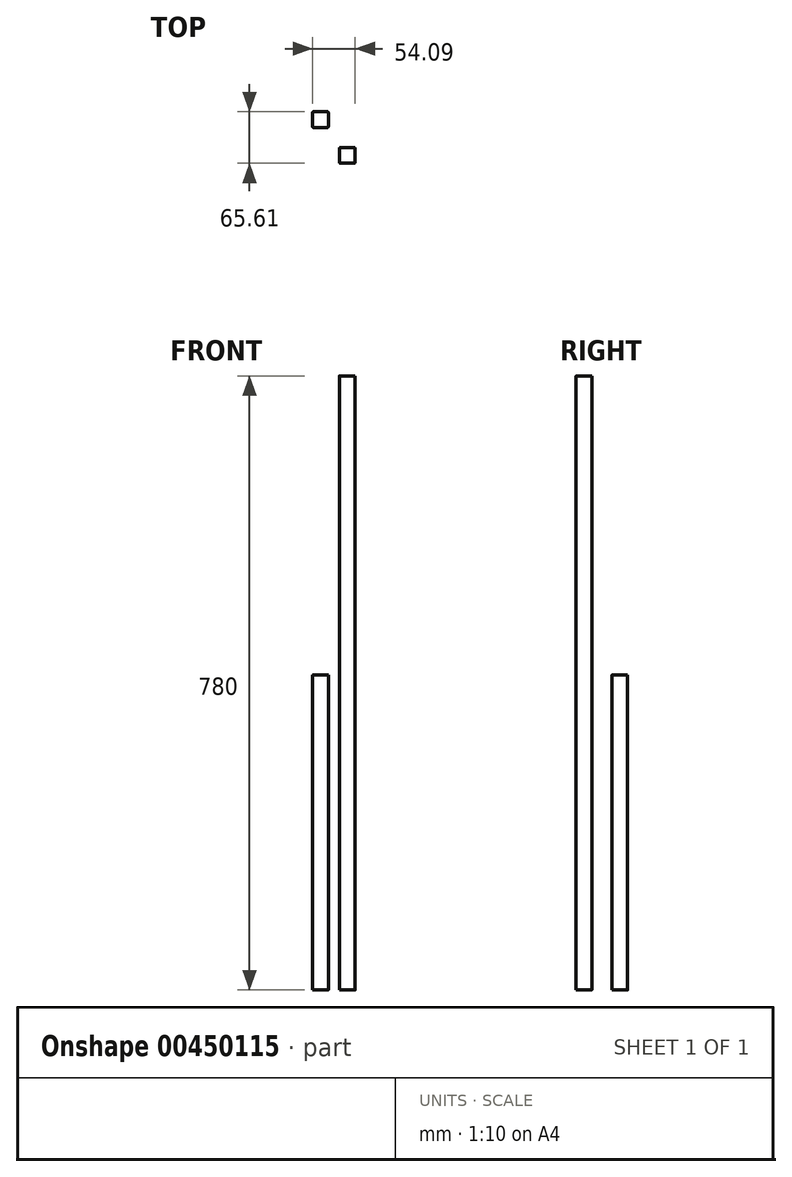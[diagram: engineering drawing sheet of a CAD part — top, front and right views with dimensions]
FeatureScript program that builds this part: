
annotation { "Feature Type Name" : "Feature", "Feature Type Description" : "" }
export const myFeature = defineFeature(function(context is Context, id is Id, definition is map)
    precondition{}
    {
        {
            assignVariable(context, id + "F0", {"name" : "legLength", "anyValue" : 780});
        }
        {
            var Q0;
            Q0=qCreatedBy(makeId("Top.planeOp"),FACE);
            var sketch = newSketch(context, id + "F1", { "sketchPlane" : qUnion([Q0])});
            skLineSegment(sketch, "E0.bottom", {"start": v(9, -10) * mm, "end": v(-9, -10) * mm});
            skLineSegment(sketch, "E0.top", {"start": v(9, 10) * mm, "end": v(-9, 10) * mm});
            skLineSegment(sketch, "E0.left", {"start": v(10, -9) * mm, "end": v(10, 9) * mm});
            skLineSegment(sketch, "E0.right", {"start": v(-10, -9) * mm, "end": v(-10, 9) * mm});
            skPoint(sketch, "E0.middle", {"position": v(0, 0) * mm});
            skPoint(sketch, "E1.visualSharp", {"position": v(-10, 10) * mm});
            skArc(sketch, "E1.filletArc", {"start": v(-9, 10) * mm, "mid": v(-9.7, 9.7) * mm, "end": v(-10, 9) * mm});
            skPoint(sketch, "E2.visualSharp", {"position": v(10, 10) * mm});
            skArc(sketch, "E2.filletArc", {"start": v(10, 9) * mm, "mid": v(9.7, 9.7) * mm, "end": v(9, 10) * mm});
            skPoint(sketch, "E3.visualSharp", {"position": v(10, -10) * mm});
            skArc(sketch, "E3.filletArc", {"start": v(9, -10) * mm, "mid": v(9.7, -9.7) * mm, "end": v(10, -9) * mm});
            skPoint(sketch, "E4.visualSharp", {"position": v(-10, -10) * mm});
            skArc(sketch, "E4.filletArc", {"start": v(-10, -9) * mm, "mid": v(-9.7, -9.7) * mm, "end": v(-9, -10) * mm});
            skLineSegment(sketch, "E5.bottom", {"start": v(24.78, 40.66) * mm, "end": v(6.78, 40.66) * mm});
            skLineSegment(sketch, "E5.top", {"start": v(24.78, 60.66) * mm, "end": v(6.78, 60.66) * mm});
            skLineSegment(sketch, "E5.left", {"start": v(25.78, 41.66) * mm, "end": v(25.78, 59.66) * mm});
            skLineSegment(sketch, "E5.right", {"start": v(5.78, 41.66) * mm, "end": v(5.78, 59.66) * mm});
            skPoint(sketch, "E5.middle", {"position": v(15.78, 50.66) * mm});
            skPoint(sketch, "E6.visualSharp", {"position": v(5.78, 60.66) * mm});
            skArc(sketch, "E6.filletArc", {"start": v(6.78, 60.66) * mm, "mid": v(6.07, 60.37) * mm, "end": v(5.78, 59.66) * mm});
            skPoint(sketch, "E7.visualSharp", {"position": v(25.78, 60.66) * mm});
            skArc(sketch, "E7.filletArc", {"start": v(25.78, 59.66) * mm, "mid": v(25.49, 60.37) * mm, "end": v(24.78, 60.66) * mm});
            skPoint(sketch, "E8.visualSharp", {"position": v(25.78, 40.66) * mm});
            skArc(sketch, "E8.filletArc", {"start": v(24.78, 40.66) * mm, "mid": v(25.49, 40.95) * mm, "end": v(25.78, 41.66) * mm});
            skPoint(sketch, "E9.visualSharp", {"position": v(5.78, 40.66) * mm});
            skArc(sketch, "E9.filletArc", {"start": v(5.78, 41.66) * mm, "mid": v(6.07, 40.95) * mm, "end": v(6.78, 40.66) * mm});
            skLineSegment(sketch, "E10.bottom", {"start": v(-25.09, 35.6) * mm, "end": v(-43.09, 35.6) * mm});
            skLineSegment(sketch, "E10.top", {"start": v(-25.09, 55.6) * mm, "end": v(-43.09, 55.6) * mm});
            skLineSegment(sketch, "E10.left", {"start": v(-24.09, 36.6) * mm, "end": v(-24.09, 54.6) * mm});
            skLineSegment(sketch, "E10.right", {"start": v(-44.09, 36.6) * mm, "end": v(-44.09, 54.6) * mm});
            skPoint(sketch, "E10.middle", {"position": v(-34.09, 45.6) * mm});
            skPoint(sketch, "E11.visualSharp", {"position": v(-44.09, 55.6) * mm});
            skArc(sketch, "E11.filletArc", {"start": v(-43.09, 55.6) * mm, "mid": v(-43.8, 55.32) * mm, "end": v(-44.09, 54.6) * mm});
            skPoint(sketch, "E12.visualSharp", {"position": v(-24.09, 55.6) * mm});
            skArc(sketch, "E12.filletArc", {"start": v(-24.09, 54.6) * mm, "mid": v(-24.38, 55.32) * mm, "end": v(-25.09, 55.6) * mm});
            skPoint(sketch, "E13.visualSharp", {"position": v(-24.09, 35.6) * mm});
            skArc(sketch, "E13.filletArc", {"start": v(-25.09, 35.6) * mm, "mid": v(-24.38, 35.9) * mm, "end": v(-24.09, 36.6) * mm});
            skPoint(sketch, "E14.visualSharp", {"position": v(-44.09, 35.6) * mm});
            skArc(sketch, "E14.filletArc", {"start": v(-44.09, 36.6) * mm, "mid": v(-43.8, 35.9) * mm, "end": v(-43.09, 35.6) * mm});
            skSolve(sketch);
        }
        {
            var Q0;
            Q0=makeQuery(id+"F1.imprint","IMPRINT",FACE,{"disambiguationData":[TD([[makeQuery(id+"F1.imprint","IMPRINT",EDGE,{"derivedFrom":sQuery(id+"F1.wireOp",EDGE,"E0.bottom")}),-1.0]])]});
            extrude(context, id + "F2", {"entities" : qUnion([Q0]), "depth" : (getVariable(context, 'legLength')) * mm});
        }
        {
            var Q0;
            Q0=makeQuery(id+"F1.imprint","IMPRINT",FACE,{"disambiguationData":[TD([[makeQuery(id+"F1.imprint","IMPRINT",EDGE,{"derivedFrom":sQuery(id+"F1.wireOp",EDGE,"E10.bottom")}),-1.0]])]});
            extrude(context, id + "F3", {"entities" : qUnion([Q0]), "depth" : 400 * mm});
        }
        {
            var Q0;
            Q0=makeQuery(id+"F2.opExtrude","SWEPT_FACE",FACE,{"disambiguationData":[OSD([sQuery(id+"F1.wireOp",EDGE,"E0.left")])]});
            var sketch = newSketch(context, id + "F4", { "sketchPlane" : qUnion([Q0])});
            skPoint(sketch, "E15", {"position": v(0, 100) * mm});
            skPoint(sketch, "E16", {"position": v(0, 460) * mm});
            skSolve(sketch);
        }
        {
            var Q0;
            Q0=makeQuery(id+"F2.opExtrude","SWEPT_FACE",FACE,{"disambiguationData":[OSD([sQuery(id+"F1.wireOp",EDGE,"E0.bottom")])]});
            var sketch = newSketch(context, id + "F5", { "sketchPlane" : qUnion([Q0])});
            skPoint(sketch, "E17", {"position": v(0, 100) * mm});
            skPoint(sketch, "E18", {"position": v(0, 0) * mm});
            skPoint(sketch, "E19", {"position": v(0, 460) * mm});
            skSolve(sketch);
        }
    });
